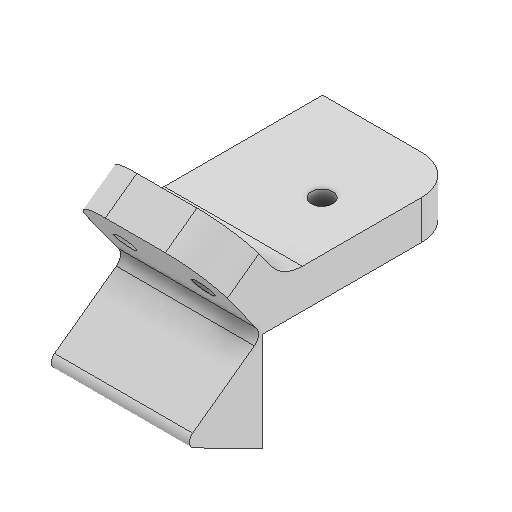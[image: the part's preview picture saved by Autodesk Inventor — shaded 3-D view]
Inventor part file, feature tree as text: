
AUTODESK INVENTOR PART (.ipt)
format: ipt  version: 2025 (Build 290162000, 162)  size: 195,584 bytes
history: native  units: mm
features: reference x6, extrude x4, sketch x4, projected_geometry x4, fillet x3, other x3
ambient origin geometry x8: Origin, YZ Plane, XZ Plane, XY Plane, X Axis, Y Axis, Z Axis, Center Point
bodies: Solid1 (feature_tree)
feature tree (24):
  extrude  "Extrusion1"  Depth=50.8mm
  extrude  "Extrusion2"  Depth=5.5mm
  extrude  "Extrusion3"  Depth=10.0mm
  extrude  "Extrusion4"  Depth=10.0mm
  fillet  "Fillet1"  Radius=5.5mm
  fillet  "Fillet2"  Radius=35.4mm
  fillet  "Fillet3"  Radius=2.6mm
  sketch  "Sketch1"  dims[d0=25.4mm d1=50.8mm]
  sketch  "Sketch2"  dims[d2=5.5mm d3=5.5mm]
  projected_geometry  "Projected Loop1"
  reference  "Reference1"
  reference  "Reference2"
  reference  "Reference3"
  reference  "Reference4"
  reference  "Reference5"
  reference  "Reference6"
  sketch  "Sketch3"  dims[d4=10.0mm d5=0.0mm d6=10.0mm]
  projected_geometry  "Projected Loop2"
  projected_geometry  "Projected Loop3"
  projected_geometry  "Projected Loop4"
  sketch  "Sketch4"  dims[d7=35.4mm d8=0.0mm d9=10.0mm d10=5.5mm d11=35.4mm d12=0.0mm d13=2.6mm d14=20.0mm d15=35.4mm d16=0.0mm d17=10.0mm d18=10.0mm d19=2.0mm]
  other  "<userpath>\Desktop\puppycat\woodhouseMK1.iam"
  other  "woodhouseMK1.iam"
  other  "horizontalStrutLower:2"
